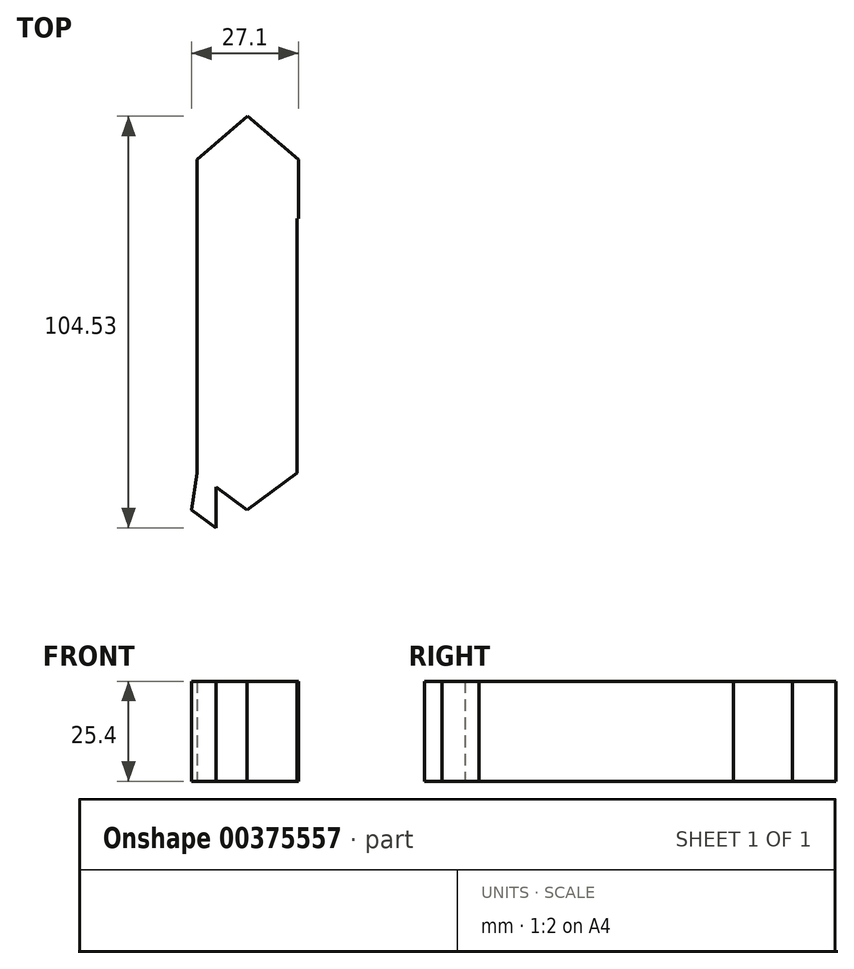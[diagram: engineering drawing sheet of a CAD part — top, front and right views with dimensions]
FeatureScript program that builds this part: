
annotation { "Feature Type Name" : "Feature", "Feature Type Description" : "" }
export const myFeature = defineFeature(function(context is Context, id is Id, definition is map)
    precondition{}
    {
        {
            var Q0;
            Q0=qCreatedBy(makeId("Top.planeOp"),FACE);
            var sketch = newSketch(context, id + "F0", { "sketchPlane" : qUnion([Q0])});
            skLineSegment(sketch, "E0.left", {"start": v(-4.75, 17.9) * mm, "end": v(-4.75, -32.9) * mm});
            skLineSegment(sketch, "E0.right", {"start": v(20.65, 17.9) * mm, "end": v(20.65, -32.9) * mm});
            skLineSegment(sketch, "E1.bottom", {"start": v(20.65, 17.9) * mm, "end": v(20.97, 17.9) * mm});
            skLineSegment(sketch, "E1.left", {"start": v(-4.75, 17.9) * mm, "end": v(-4.75, 32.9) * mm});
            skLineSegment(sketch, "E1.right", {"start": v(20.97, 17.9) * mm, "end": v(20.97, 32.9) * mm});
            skLineSegment(sketch, "E2", {"start": v(-4.75, 32.9) * mm, "end": v(8.1, 43.88) * mm});
            skPoint(sketch, "E2.endSnap0", {"position": v(8.1, 32.9) * mm});
            skLineSegment(sketch, "E3", {"start": v(8.1, 43.88) * mm, "end": v(20.97, 32.9) * mm});
            skLineSegment(sketch, "E4.left", {"start": v(-4.75, -32.9) * mm, "end": v(-4.75, -46.78) * mm});
            skLineSegment(sketch, "E4.right", {"start": v(20.65, -32.9) * mm, "end": v(20.65, -46.78) * mm});
            skLineSegment(sketch, "E5", {"start": v(0, -50.28) * mm, "end": v(7.95, -56.14) * mm});
            skPoint(sketch, "E5.endSnap0", {"position": v(7.95, -46.78) * mm});
            skLineSegment(sketch, "E6", {"start": v(7.95, -56.14) * mm, "end": v(20.65, -46.78) * mm});
            skLineSegment(sketch, "E7", {"start": v(0, -50.28) * mm, "end": v(0, -60.65) * mm});
            skLineSegment(sketch, "E8", {"start": v(0, -60.65) * mm, "end": v(-6.13, -56.14) * mm});
            skLineSegment(sketch, "E9", {"start": v(-6.13, -56.14) * mm, "end": v(-4.75, -46.78) * mm});
            skSolve(sketch);
        }
        {
            var Q0;
            Q0 = qSketchRegion(id + "F0", true);
            extrude(context, id + "F1", {"entities" : qUnion([Q0]), "depth" : 25.4 * mm});
        }
    });
